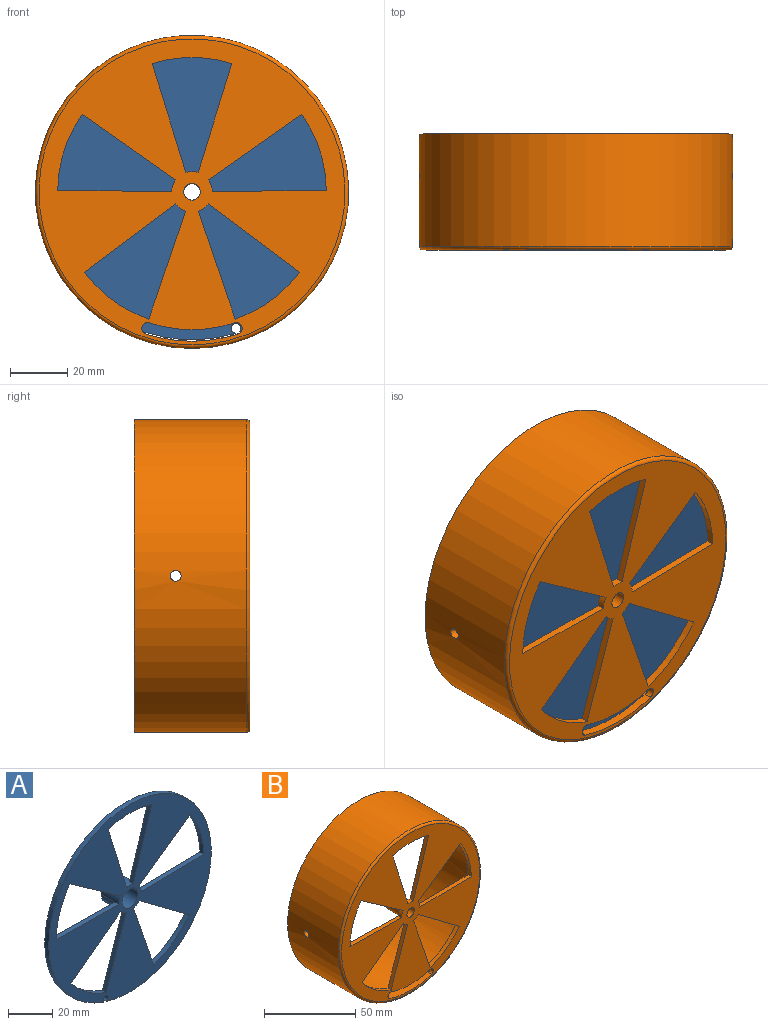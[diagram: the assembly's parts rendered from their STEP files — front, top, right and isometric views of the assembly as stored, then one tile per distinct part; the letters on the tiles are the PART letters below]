
ASSEMBLY  parts=2 mates=1
PART A: 23 faces, bbox 103.8x11.2x103.8 mm
  f0: plane 103.76x103.76mm, normal (0,-1,0), area 5091.3mm2, adj f2,f3,f4,f5,f6,f7,f8,f9
  f1: plane 103.76x103.76mm, normal (0,1,0), area 5013.1mm2, adj f2,f3,f4,f5,f6,f7,f8,f9
  f2: cylinder r=51.88mm len=103.76mm, axis (0,-1,0), area 823.9mm2, adj f0,f1,f22
  f3: plane 38.19x11.81mm, normal (-0.96,0,0.3), area 101.5mm2, adj f0,f1,f5,f15
  f4: plane 38.19x11.81mm, normal (0.96,0,0.3), area 101.5mm2, adj f0,f1,f5,f15
  f5: cylinder r=47.12mm len=27.94mm, axis (0,1,0), area 72.1mm2, adj f0,f1,f3,f4
  f6: plane 39.97x2.54mm, normal (0.01,0,1), area 101.5mm2, adj f0,f1,f7,f15
  f7: cylinder r=47.12mm len=26.57mm, axis (0,1,0), area 72.1mm2, adj f0,f1,f6,f8
  f8: plane 32.67x23.03mm, normal (-0.58,0,-0.82), area 101.5mm2, adj f0,f1,f7,f15
  f9: plane 37.84x12.89mm, normal (-0.95,0,0.32), area 101.5mm2, adj f0,f1,f10,f15
  f10: cylinder r=47.12mm len=22.6mm, axis (0,1,0), area 72.1mm2, adj f0,f1,f9,f11
  f11: plane 32x23.95mm, normal (0.6,0,-0.8), area 101.5mm2, adj f0,f1,f10,f15
  f12: plane 32x23.95mm, normal (-0.6,0,-0.8), area 101.5mm2, adj f0,f1,f13,f15
  f13: cylinder r=47.12mm len=22.6mm, axis (0,1,0), area 72.1mm2, adj f0,f1,f12,f14
  f14: plane 37.84x12.89mm, normal (0.95,0,0.32), area 101.5mm2, adj f0,f1,f13,f15
  f15: cylinder r=7.14mm len=14.29mm, axis (0,1,0), area 403.7mm2, adj f0,f1,f3,f4,f6,f8,f9,f11
  f16: plane 32.67x23.03mm, normal (0.58,0,-0.82), area 101.5mm2, adj f0,f1,f15,f17
  f17: cylinder r=47.12mm len=26.57mm, axis (0,1,0), area 72.1mm2, adj f0,f1,f16,f18
  f18: plane 39.97x2.54mm, normal (-0.01,0,1), area 101.5mm2, adj f0,f1,f15,f17
  f19: cylinder r=5.11mm len=11.18mm, axis (0,1,0), area 359mm2, adj f0,f20
  f20: plane 14.3x14.29mm, normal (0,1,0), area 78.2mm2, adj f15,f19,f21
  f21: extruded ~8.64x4.29mm, area 39.6mm2, adj f1,f15,f20
  f22: cylinder r=1.71mm len=3.43mm, axis (0,-1,0), area 23.2mm2, adj f0,f1,f2
PART B: 35 faces, bbox 118.9x40.6x118.9 mm
  f0: plane 104.78x102.21mm, normal (0,1,0), area 5140.7mm2, adj f4,f5,f6,f7,f8,f9,f10,f11
  f1: plane 107.32x107.32mm, normal (0,-1,0), area 5603.9mm2, adj f4,f5,f6,f7,f8,f9,f10,f11
  f2: cylinder r=54.93mm len=109.86mm, axis (0,1,0), area 13564.4mm2, adj f3,f31,f32,f34
  f3: plane 109.86x109.86mm, normal (0,1,0), area 433.2mm2, adj f2,f33
  f4: cylinder r=52.39mm len=104.78mm, axis (0,1,0), area 11877.6mm2, adj f0,f1,f29,f30,f31,f32,f33
  f5: plane 38.19x11.81mm, normal (-0.96,0,0.3), area 101.5mm2, adj f0,f1,f6,f8
  f6: cylinder r=7.14mm len=4.32mm, axis (0,1,0), area 11.1mm2, adj f0,f1,f5,f7
  f7: plane 38.19x11.81mm, normal (0.96,0,0.3), area 101.5mm2, adj f0,f1,f6,f8
  f8: cylinder r=47.12mm len=27.94mm, axis (0,1,0), area 72.1mm2, adj f0,f1,f5,f7
  f9: cylinder r=7.14mm len=4.11mm, axis (0,1,0), area 11.1mm2, adj f0,f1,f10,f12
  f10: plane 39.97x2.54mm, normal (0.01,0,1), area 101.5mm2, adj f0,f1,f9,f11
  f11: cylinder r=47.12mm len=26.57mm, axis (0,1,0), area 72.1mm2, adj f0,f1,f10,f12
  f12: plane 32.67x23.03mm, normal (-0.58,0,-0.82), area 101.5mm2, adj f0,f1,f9,f11
  f13: plane 37.84x12.89mm, normal (-0.95,0,0.32), area 101.5mm2, adj f0,f1,f14,f16
  f14: cylinder r=47.12mm len=22.6mm, axis (0,1,0), area 72.1mm2, adj f0,f1,f13,f15
  f15: plane 32x23.95mm, normal (0.6,0,-0.8), area 101.5mm2, adj f0,f1,f14,f16
  f16: cylinder r=7.14mm len=3.49mm, axis (0,1,0), area 11.1mm2, adj f0,f1,f13,f15
  f17: cylinder r=7.14mm len=3.49mm, axis (0,1,0), area 11.1mm2, adj f0,f1,f18,f20
  f18: plane 32x23.95mm, normal (-0.6,0,-0.8), area 101.5mm2, adj f0,f1,f17,f19
  f19: cylinder r=47.12mm len=22.6mm, axis (0,1,0), area 72.1mm2, adj f0,f1,f18,f20
  f20: plane 37.84x12.89mm, normal (0.95,0,0.32), area 101.5mm2, adj f0,f1,f17,f19
  f21: cylinder r=7.14mm len=4.11mm, axis (0,1,0), area 11.1mm2, adj f0,f1,f22,f24
  f22: plane 32.67x23.03mm, normal (0.58,0,-0.82), area 101.5mm2, adj f0,f1,f21,f23
  f23: cylinder r=47.12mm len=26.57mm, axis (0,1,0), area 72.1mm2, adj f0,f1,f22,f24
  f24: plane 39.97x2.54mm, normal (-0.01,0,1), area 101.5mm2, adj f0,f1,f21,f23
  f25: cylinder r=2.9mm len=13.97mm, axis (0,-1,0), area 254.7mm2, adj f1,f27
  f26: cylinder r=4.6mm len=11.43mm, axis (0,-1,0), area 330.6mm2, adj f0,f27
  f27: plane 9.21x9.21mm, normal (0,1,0), area 40.1mm2, adj f25,f26
  f28: cylinder r=48.32mm len=29.87mm, axis (0,-1,0), area 77.1mm2, adj f0,f1,f29,f30
  f29: cylinder r=2.03mm len=3.96mm, axis (0,-1,0), area 16.2mm2, adj f0,f1,f4,f28
  f30: cylinder r=2.03mm len=3.96mm, axis (0,-1,0), area 16.2mm2, adj f0,f1,f4,f28
  f31: cylinder r=1.91mm len=3.81mm, axis (1,0,0), area 30.4mm2, adj f2,f4
  f32: cylinder r=1.91mm len=3.81mm, axis (1,0,0), area 30.4mm2, adj f2,f4
  f33: cone r=53.66mm half-angle=30deg, axis (0,1,0), area 846.2mm2, adj f3,f4
  f34: torus R=53.66mm, axis (0,-1,0), area 682.7mm2, adj f1,f2
PLACE A rot(axis=(0,-1,0),35.9deg) t=(0,-0.25,0)mm
PLACE B at identity fixed
MATE revolute A.f17 <-> B.f23  axis (0,-1,0) through (0,-38.1,0)mm
